# Revit family: Ginestra 300
name_source: partatom
category: Lighting Fixtures
units: mm (PartAtom-declared; Revit-internal decimal feet)

## family parameters
Always vertical = Yes
Cut with Voids When Loaded = No
Host = Ceiling
Light Source = No
OmniClass Number = 23.80.70.11
OmniClass Title = Luminaries for Internal Lighting
Part Type = Normal
Room Calculation Point = No
Round Connector Dimension = Use Diameter
Shared = No

## types (1)
- CE
    ADA compliant = Not Applicable
    Default Elevation = 0 mm  [stored 0 ft]
    Dimmable = Yes
    Dimming Method = Lamp dependent
    Driver Included = Not Applicable
    Driver Required = No
    Efficacy (lm/w) = Lamp dependent
    Electrical Class = II
    Lamp = E27
    Light Source Fixed = Replaceable
    Location Rating = IP20
    Main Finish = Various
    Main Material = Steel
    Max Drop (pendants) = 2055
    Power (Watts) = Lamp dependent
    Product Location = Indoor
    Product Name = Ginestra 300
    Product SKU = 1361xxx
    drop = 1800 mm  [stored 5.90551 ft]
    drop (min 10, max 3000) = 10 mm  [stored 0.0328084 ft]

note: [stored X ft] marks values corroborated as IEEE doubles in the binary element streams (Revit-internal decimal feet)

## geometry (parser evidence)
native form markers: Sweep x3
no freeform markers — native parametric forms only
